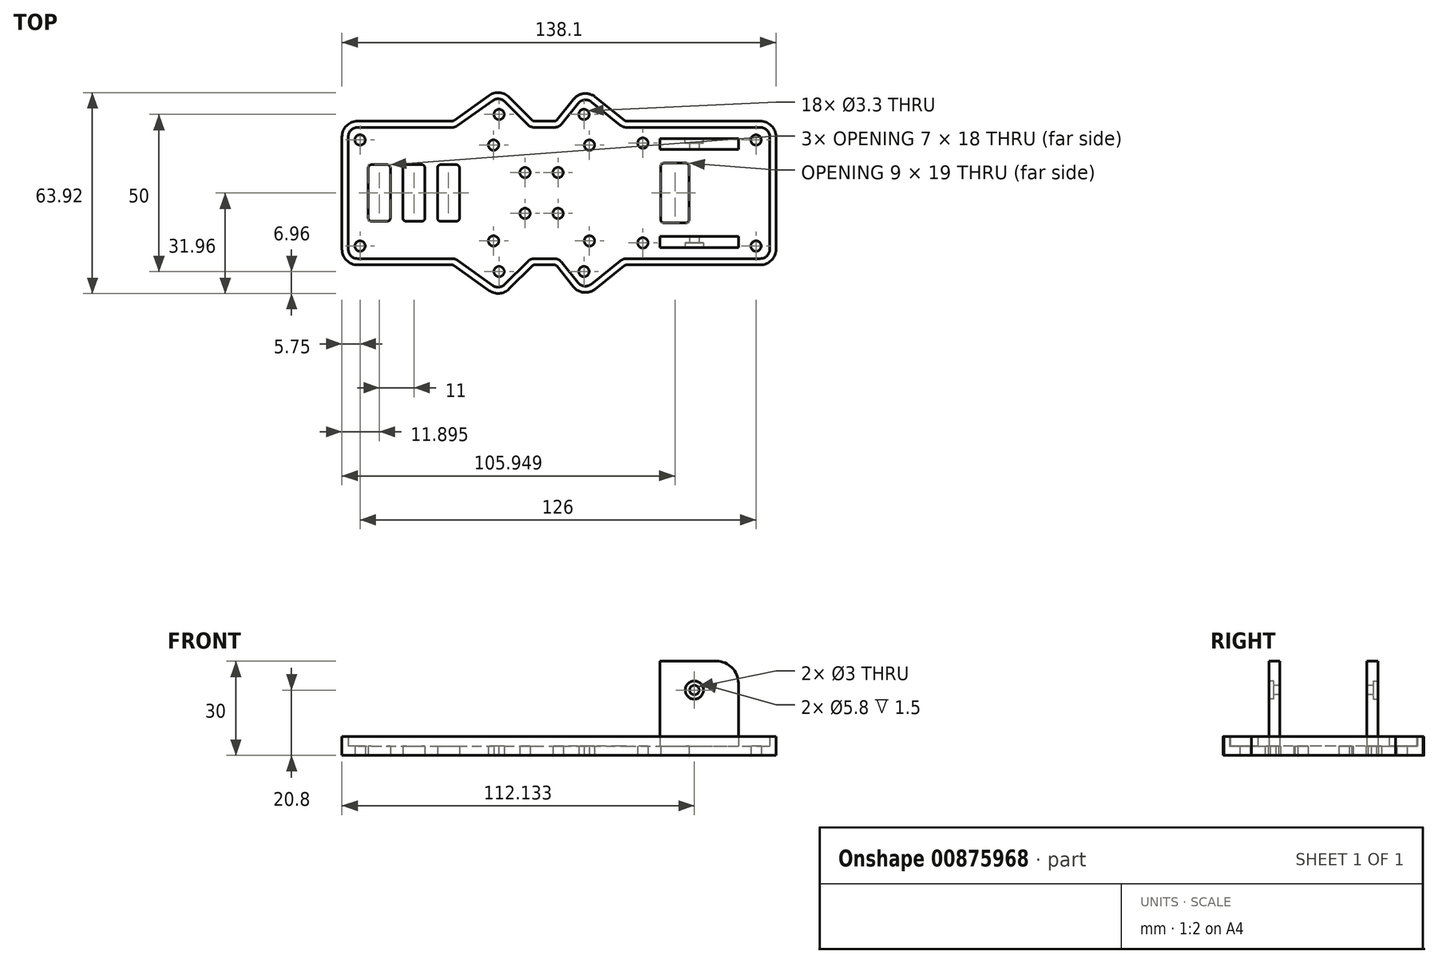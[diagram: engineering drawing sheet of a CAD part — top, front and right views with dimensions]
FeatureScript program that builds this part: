
annotation { "Feature Type Name" : "Feature", "Feature Type Description" : "" }
export const myFeature = defineFeature(function(context is Context, id is Id, definition is map)
    precondition{}
    {
        {
            var Q0;
            Q0=qCreatedBy(makeId("Top.planeOp"),FACE);
            var sketch = newSketch(context, id + "F0", { "sketchPlane" : qUnion([Q0])});
            skLineSegment(sketch, "E0.bottom", {"start": v(-58.5, 20.88) * mm, "end": v(-28.46, 20.88) * mm});
            skLineSegment(sketch, "E0.top", {"start": v(-58.5, -20.88) * mm, "end": v(-28.46, -20.88) * mm});
            skLineSegment(sketch, "E0.left", {"start": v(-61.5, 17.88) * mm, "end": v(-61.5, -17.88) * mm});
            skLineSegment(sketch, "E0.right", {"start": v(72.6, 17.88) * mm, "end": v(72.6, -17.88) * mm});
            skCircle(sketch, "E1", {"center": v(-5.25, 6.5) * mm, "radius": 1.65 * mm});
            skCircle(sketch, "E2.1.0.0", {"center": v(5.25, 6.5) * mm, "radius": 1.65 * mm});
            skCircle(sketch, "E3.0.1.0", {"center": v(-5.25, -6.5) * mm, "radius": 1.65 * mm});
            skCircle(sketch, "E3.0.1.1", {"center": v(5.25, -6.5) * mm, "radius": 1.65 * mm});
            skCircle(sketch, "E4", {"center": v(-15.25, 15.25) * mm, "radius": 1.65 * mm});
            skCircle(sketch, "E5", {"center": v(15.25, 15.25) * mm, "radius": 1.65 * mm});
            skCircle(sketch, "E6", {"center": v(15.25, -15.25) * mm, "radius": 1.65 * mm});
            skCircle(sketch, "E7", {"center": v(-15.25, -15.25) * mm, "radius": 1.65 * mm});
            skCircle(sketch, "E8", {"center": v(-13.5, 25) * mm, "radius": 1.65 * mm});
            skCircle(sketch, "E9.0.1.0", {"center": v(-13.5, -25) * mm, "radius": 1.65 * mm});
            skCircle(sketch, "E9.1.0.0", {"center": v(13.5, 25) * mm, "radius": 1.65 * mm});
            skCircle(sketch, "E9.1.1.0", {"center": v(13.5, -25) * mm, "radius": 1.65 * mm});
            skLineSegment(sketch, "E9.direction1", {"start": v(-13.5, 25) * mm, "end": v(13.5, 25) * mm, "construction": true});
            skLineSegment(sketch, "E9.direction2", {"start": v(-13.5, 25) * mm, "end": v(-13.5, -25) * mm, "construction": true});
            skCircle(sketch, "E10", {"center": v(-57.75, 16.88) * mm, "radius": 1.65 * mm});
            skCircle(sketch, "E11.0.1.0", {"center": v(-57.75, -16.88) * mm, "radius": 1.65 * mm});
            skLineSegment(sketch, "E11.direction2", {"start": v(-57.75, 16.88) * mm, "end": v(-57.75, -16.88) * mm, "construction": true});
            skLineSegment(sketch, "E12", {"start": v(-26.72, 21.43) * mm, "end": v(-15.57, 29.4) * mm});
            skLineSegment(sketch, "E13", {"start": v(-11.7, 29.08) * mm, "end": v(-4.38, 21.75) * mm});
            skLineSegment(sketch, "E14", {"start": v(-2.26, 20.88) * mm, "end": v(4.1, 20.88) * mm});
            skLineSegment(sketch, "E15", {"start": v(6.45, 22) * mm, "end": v(11.67, 28.53) * mm});
            skLineSegment(sketch, "E16", {"start": v(15.9, 29) * mm, "end": v(25.16, 21.54) * mm});
            skLineSegment(sketch, "E17.trimOffspring", {"start": v(27.04, 20.88) * mm, "end": v(69.6, 20.88) * mm});
            skLineSegment(sketch, "E18", {"start": v(-26.72, -21.43) * mm, "end": v(-15.57, -29.4) * mm});
            skLineSegment(sketch, "E19", {"start": v(-11.7, -29.08) * mm, "end": v(-4.38, -21.75) * mm});
            skLineSegment(sketch, "E20", {"start": v(25.16, -21.53) * mm, "end": v(15.85, -29) * mm});
            skLineSegment(sketch, "E21", {"start": v(11.63, -28.52) * mm, "end": v(6.45, -22) * mm});
            skLineSegment(sketch, "E22.trimOffspring", {"start": v(-2.26, -20.88) * mm, "end": v(4.1, -20.88) * mm});
            skLineSegment(sketch, "E23.trimOffspring", {"start": v(27.04, -20.88) * mm, "end": v(69.6, -20.88) * mm});
            skPoint(sketch, "E24.visualSharp", {"position": v(-61.5, 20.88) * mm});
            skArc(sketch, "E24.filletArc", {"start": v(-58.5, 20.88) * mm, "mid": v(-60.62, 20) * mm, "end": v(-61.5, 17.88) * mm});
            skPoint(sketch, "E25.visualSharp", {"position": v(-61.5, -20.88) * mm});
            skArc(sketch, "E25.filletArc", {"start": v(-61.5, -17.88) * mm, "mid": v(-60.62, -20) * mm, "end": v(-58.5, -20.88) * mm});
            skPoint(sketch, "E26.visualSharp", {"position": v(-27.5, 20.88) * mm});
            skArc(sketch, "E26.filletArc", {"start": v(-28.46, 20.88) * mm, "mid": v(-27.55, 21.02) * mm, "end": v(-26.72, 21.43) * mm});
            skPoint(sketch, "E27.visualSharp", {"position": v(-27.5, -20.88) * mm});
            skArc(sketch, "E27.filletArc", {"start": v(-26.72, -21.43) * mm, "mid": v(-27.55, -21.02) * mm, "end": v(-28.46, -20.88) * mm});
            skPoint(sketch, "E28.visualSharp", {"position": v(-13.5, -30.88) * mm});
            skArc(sketch, "E28.filletArc", {"start": v(-15.57, -29.4) * mm, "mid": v(-13.58, -29.95) * mm, "end": v(-11.7, -29.08) * mm});
            skPoint(sketch, "E29.visualSharp", {"position": v(-3.5, -20.88) * mm});
            skArc(sketch, "E29.filletArc", {"start": v(-2.26, -20.88) * mm, "mid": v(-3.4, -21.1) * mm, "end": v(-4.38, -21.75) * mm});
            skPoint(sketch, "E30.visualSharp", {"position": v(5.55, -20.88) * mm});
            skArc(sketch, "E30.filletArc", {"start": v(6.45, -22) * mm, "mid": v(5.4, -21.17) * mm, "end": v(4.1, -20.88) * mm});
            skPoint(sketch, "E31.visualSharp", {"position": v(13.5, -30.88) * mm});
            skArc(sketch, "E31.filletArc", {"start": v(11.63, -28.52) * mm, "mid": v(13.64, -29.63) * mm, "end": v(15.85, -29) * mm});
            skPoint(sketch, "E32.visualSharp", {"position": v(25.99, -20.88) * mm});
            skArc(sketch, "E32.filletArc", {"start": v(27.04, -20.88) * mm, "mid": v(26.05, -21.04) * mm, "end": v(25.16, -21.53) * mm});
            skPoint(sketch, "E33.visualSharp", {"position": v(-3.5, 20.88) * mm});
            skArc(sketch, "E33.filletArc", {"start": v(-4.38, 21.75) * mm, "mid": v(-3.4, 21.1) * mm, "end": v(-2.26, 20.88) * mm});
            skPoint(sketch, "E34.visualSharp", {"position": v(5.55, 20.88) * mm});
            skArc(sketch, "E34.filletArc", {"start": v(4.1, 20.88) * mm, "mid": v(5.4, 21.17) * mm, "end": v(6.45, 22) * mm});
            skPoint(sketch, "E35.visualSharp", {"position": v(13.55, 30.88) * mm});
            skArc(sketch, "E35.filletArc", {"start": v(15.9, 29) * mm, "mid": v(13.69, 29.63) * mm, "end": v(11.67, 28.53) * mm});
            skPoint(sketch, "E36.visualSharp", {"position": v(25.99, 20.88) * mm});
            skArc(sketch, "E36.filletArc", {"start": v(25.16, 21.54) * mm, "mid": v(26.05, 21.05) * mm, "end": v(27.04, 20.88) * mm});
            skPoint(sketch, "E37.visualSharp", {"position": v(72.6, 20.88) * mm});
            skArc(sketch, "E37.filletArc", {"start": v(72.6, 17.88) * mm, "mid": v(71.72, 20) * mm, "end": v(69.6, 20.88) * mm});
            skPoint(sketch, "E38.visualSharp", {"position": v(72.6, -20.87) * mm});
            skArc(sketch, "E38.filletArc", {"start": v(69.6, -20.87) * mm, "mid": v(71.72, -20) * mm, "end": v(72.6, -17.88) * mm});
            skPoint(sketch, "E39.visualSharp", {"position": v(-13.5, 30.88) * mm});
            skArc(sketch, "E39.filletArc", {"start": v(-11.7, 29.08) * mm, "mid": v(-13.58, 29.95) * mm, "end": v(-15.57, 29.4) * mm});
            skCircle(sketch, "E40", {"center": v(32.25, 15.88) * mm, "radius": 1.65 * mm});
            skCircle(sketch, "E41", {"center": v(68.25, 16.88) * mm, "radius": 1.65 * mm});
            skCircle(sketch, "E42.0.1.0", {"center": v(32.25, -15.88) * mm, "radius": 1.65 * mm});
            skLineSegment(sketch, "E42.direction1", {"start": v(32.25, 15.88) * mm, "end": v(39.65, 15.88) * mm, "construction": true});
            skLineSegment(sketch, "E42.direction2", {"start": v(32.25, 15.88) * mm, "end": v(32.25, -15.88) * mm, "construction": true});
            skCircle(sketch, "E43.0.1.0", {"center": v(68.25, -16.88) * mm, "radius": 1.65 * mm});
            skLineSegment(sketch, "E43.direction1", {"start": v(68.25, 16.88) * mm, "end": v(93.25, 16.88) * mm, "construction": true});
            skLineSegment(sketch, "E43.direction2", {"start": v(68.25, 16.88) * mm, "end": v(68.25, -16.88) * mm, "construction": true});
            skArc(sketch, "E44.0", {"start": v(-58.5, 22.88) * mm, "mid": v(-62.04, 21.41) * mm, "end": v(-63.5, 17.88) * mm});
            skLineSegment(sketch, "E44.1", {"start": v(-63.5, 17.88) * mm, "end": v(-63.5, -17.88) * mm});
            skArc(sketch, "E44.2", {"start": v(-63.5, -17.88) * mm, "mid": v(-62.04, -21.41) * mm, "end": v(-58.5, -22.88) * mm});
            skLineSegment(sketch, "E44.3", {"start": v(-58.5, -22.88) * mm, "end": v(-28.46, -22.88) * mm});
            skArc(sketch, "E44.4", {"start": v(-27.88, -23.06) * mm, "mid": v(-28.16, -22.92) * mm, "end": v(-28.46, -22.87) * mm});
            skLineSegment(sketch, "E44.5", {"start": v(-27.88, -23.06) * mm, "end": v(-16.73, -31.03) * mm});
            skArc(sketch, "E44.6", {"start": v(-16.73, -31.03) * mm, "mid": v(-13.41, -31.94) * mm, "end": v(-10.29, -30.5) * mm});
            skLineSegment(sketch, "E44.7", {"start": v(-10.29, -30.5) * mm, "end": v(-2.96, -23.17) * mm});
            skArc(sketch, "E44.8", {"start": v(-2.26, -22.88) * mm, "mid": v(-2.64, -22.95) * mm, "end": v(-2.96, -23.17) * mm});
            skLineSegment(sketch, "E44.9", {"start": v(17.15, 30.55) * mm, "end": v(26.42, 23.1) * mm});
            skArc(sketch, "E44.10", {"start": v(17.15, 30.55) * mm, "mid": v(13.47, 31.62) * mm, "end": v(10.1, 29.78) * mm});
            skLineSegment(sketch, "E44.11", {"start": v(4.89, 23.25) * mm, "end": v(10.1, 29.78) * mm});
            skArc(sketch, "E44.12", {"start": v(4.1, 22.88) * mm, "mid": v(4.54, 22.97) * mm, "end": v(4.89, 23.25) * mm});
            skLineSegment(sketch, "E44.13", {"start": v(-2.26, 22.88) * mm, "end": v(4.1, 22.88) * mm});
            skArc(sketch, "E44.14", {"start": v(-2.96, 23.17) * mm, "mid": v(-2.64, 22.95) * mm, "end": v(-2.26, 22.88) * mm});
            skArc(sketch, "E44.15", {"start": v(-28.46, 22.88) * mm, "mid": v(-28.16, 22.92) * mm, "end": v(-27.88, 23.06) * mm});
            skLineSegment(sketch, "E44.16", {"start": v(-27.88, 23.06) * mm, "end": v(-16.73, 31.03) * mm});
            skArc(sketch, "E44.17", {"start": v(-10.29, 30.5) * mm, "mid": v(-13.41, 31.94) * mm, "end": v(-16.73, 31.03) * mm});
            skLineSegment(sketch, "E44.18", {"start": v(-10.29, 30.5) * mm, "end": v(-2.96, 23.17) * mm});
            skArc(sketch, "E44.19", {"start": v(26.42, 23.1) * mm, "mid": v(26.71, 22.93) * mm, "end": v(27.04, 22.88) * mm});
            skLineSegment(sketch, "E44.20", {"start": v(27.04, 22.88) * mm, "end": v(69.6, 22.88) * mm});
            skArc(sketch, "E44.21", {"start": v(74.6, 17.88) * mm, "mid": v(73.14, 21.41) * mm, "end": v(69.6, 22.88) * mm});
            skLineSegment(sketch, "E44.22", {"start": v(74.6, 17.88) * mm, "end": v(74.6, -17.88) * mm});
            skArc(sketch, "E44.23", {"start": v(69.6, -22.88) * mm, "mid": v(73.14, -21.41) * mm, "end": v(74.6, -17.88) * mm});
            skLineSegment(sketch, "E44.24", {"start": v(27.04, -22.88) * mm, "end": v(69.6, -22.88) * mm});
            skArc(sketch, "E44.25", {"start": v(27.04, -22.88) * mm, "mid": v(26.7, -22.93) * mm, "end": v(26.41, -23.1) * mm});
            skLineSegment(sketch, "E44.26", {"start": v(26.41, -23.1) * mm, "end": v(17.1, -30.55) * mm});
            skArc(sketch, "E44.27", {"start": v(10.06, -29.76) * mm, "mid": v(13.42, -31.62) * mm, "end": v(17.1, -30.55) * mm});
            skLineSegment(sketch, "E44.28", {"start": v(-58.5, 22.88) * mm, "end": v(-28.46, 22.88) * mm});
            skLineSegment(sketch, "E44.29", {"start": v(10.06, -29.76) * mm, "end": v(4.89, -23.25) * mm});
            skArc(sketch, "E44.30", {"start": v(4.89, -23.25) * mm, "mid": v(4.54, -22.97) * mm, "end": v(4.1, -22.88) * mm});
            skLineSegment(sketch, "E44.31", {"start": v(-2.26, -22.88) * mm, "end": v(4.1, -22.88) * mm});
            skLineSegment(sketch, "E45.bottom", {"start": v(-54.1, 9) * mm, "end": v(-49.1, 9) * mm});
            skLineSegment(sketch, "E45.top", {"start": v(-54.1, -9) * mm, "end": v(-49.1, -9) * mm});
            skLineSegment(sketch, "E45.left", {"start": v(-55.1, 8) * mm, "end": v(-55.1, -8) * mm});
            skLineSegment(sketch, "E45.right", {"start": v(-48.1, 8) * mm, "end": v(-48.1, -8) * mm});
            skLineSegment(sketch, "E46.1.0.0", {"start": v(-44.1, 8) * mm, "end": v(-44.1, -8) * mm});
            skLineSegment(sketch, "E46.1.0.1", {"start": v(-43.1, 9) * mm, "end": v(-38.1, 9) * mm});
            skLineSegment(sketch, "E46.1.0.2", {"start": v(-37.1, 8) * mm, "end": v(-37.1, -8) * mm});
            skLineSegment(sketch, "E46.1.0.3", {"start": v(-43.1, -9) * mm, "end": v(-38.1, -9) * mm});
            skLineSegment(sketch, "E46.2.0.0", {"start": v(-33.1, 8) * mm, "end": v(-33.1, -8) * mm});
            skLineSegment(sketch, "E46.2.0.1", {"start": v(-32.1, 9) * mm, "end": v(-27.1, 9) * mm});
            skLineSegment(sketch, "E46.2.0.2", {"start": v(-26.1, 8) * mm, "end": v(-26.1, -8) * mm});
            skLineSegment(sketch, "E46.2.0.3", {"start": v(-32.1, -9) * mm, "end": v(-27.1, -9) * mm});
            skLineSegment(sketch, "E46.direction1", {"start": v(-55.1, -9) * mm, "end": v(-44.1, -9) * mm, "construction": true});
            skPoint(sketch, "E47.visualSharp", {"position": v(-55.1, 9) * mm});
            skArc(sketch, "E47.filletArc", {"start": v(-54.1, 9) * mm, "mid": v(-54.81, 8.7) * mm, "end": v(-55.1, 8) * mm});
            skPoint(sketch, "E48.visualSharp", {"position": v(-48.1, 9) * mm});
            skArc(sketch, "E48.filletArc", {"start": v(-48.1, 8) * mm, "mid": v(-48.4, 8.7) * mm, "end": v(-49.1, 9) * mm});
            skPoint(sketch, "E49.visualSharp", {"position": v(-55.1, -9) * mm});
            skArc(sketch, "E49.filletArc", {"start": v(-55.1, -8) * mm, "mid": v(-54.81, -8.7) * mm, "end": v(-54.1, -9) * mm});
            skPoint(sketch, "E50.visualSharp", {"position": v(-48.1, -9) * mm});
            skArc(sketch, "E50.filletArc", {"start": v(-49.1, -9) * mm, "mid": v(-48.4, -8.7) * mm, "end": v(-48.1, -8) * mm});
            skPoint(sketch, "E51.visualSharp", {"position": v(-44.1, 9) * mm});
            skArc(sketch, "E51.filletArc", {"start": v(-43.1, 9) * mm, "mid": v(-43.81, 8.7) * mm, "end": v(-44.1, 8) * mm});
            skPoint(sketch, "E52.visualSharp", {"position": v(-37.1, 9) * mm});
            skArc(sketch, "E52.filletArc", {"start": v(-37.1, 8) * mm, "mid": v(-37.4, 8.7) * mm, "end": v(-38.1, 9) * mm});
            skPoint(sketch, "E53.visualSharp", {"position": v(-44.1, -9) * mm});
            skArc(sketch, "E53.filletArc", {"start": v(-44.1, -8) * mm, "mid": v(-43.81, -8.7) * mm, "end": v(-43.1, -9) * mm});
            skPoint(sketch, "E54.visualSharp", {"position": v(-37.1, -9) * mm});
            skArc(sketch, "E54.filletArc", {"start": v(-38.1, -9) * mm, "mid": v(-37.4, -8.7) * mm, "end": v(-37.1, -8) * mm});
            skPoint(sketch, "E55.visualSharp", {"position": v(-33.1, -9) * mm});
            skArc(sketch, "E55.filletArc", {"start": v(-33.1, -8) * mm, "mid": v(-32.81, -8.7) * mm, "end": v(-32.1, -9) * mm});
            skPoint(sketch, "E56.visualSharp", {"position": v(-26.1, -9) * mm});
            skArc(sketch, "E56.filletArc", {"start": v(-27.1, -9) * mm, "mid": v(-26.4, -8.7) * mm, "end": v(-26.1, -8) * mm});
            skPoint(sketch, "E57.visualSharp", {"position": v(-26.1, 9) * mm});
            skArc(sketch, "E57.filletArc", {"start": v(-26.1, 8) * mm, "mid": v(-26.4, 8.7) * mm, "end": v(-27.1, 9) * mm});
            skPoint(sketch, "E58.visualSharp", {"position": v(-33.1, 9) * mm});
            skArc(sketch, "E58.filletArc", {"start": v(-32.1, 9) * mm, "mid": v(-32.81, 8.7) * mm, "end": v(-33.1, 8) * mm});
            skLineSegment(sketch, "E59.bottom", {"start": v(38.95, 9.5) * mm, "end": v(45.95, 9.5) * mm});
            skLineSegment(sketch, "E59.top", {"start": v(38.95, -9.5) * mm, "end": v(45.95, -9.5) * mm});
            skLineSegment(sketch, "E59.left", {"start": v(37.95, 8.5) * mm, "end": v(37.95, -8.5) * mm});
            skLineSegment(sketch, "E59.right", {"start": v(46.95, 8.5) * mm, "end": v(46.95, -8.5) * mm});
            skPoint(sketch, "E60.visualSharp", {"position": v(37.95, 9.5) * mm});
            skArc(sketch, "E60.filletArc", {"start": v(38.95, 9.5) * mm, "mid": v(38.24, 9.2) * mm, "end": v(37.95, 8.5) * mm});
            skPoint(sketch, "E61.visualSharp", {"position": v(46.95, 9.5) * mm});
            skArc(sketch, "E61.filletArc", {"start": v(46.95, 8.5) * mm, "mid": v(46.66, 9.2) * mm, "end": v(45.95, 9.5) * mm});
            skPoint(sketch, "E62.visualSharp", {"position": v(46.95, -9.5) * mm});
            skArc(sketch, "E62.filletArc", {"start": v(45.95, -9.5) * mm, "mid": v(46.66, -9.2) * mm, "end": v(46.95, -8.5) * mm});
            skPoint(sketch, "E63.visualSharp", {"position": v(37.95, -9.5) * mm});
            skArc(sketch, "E63.filletArc", {"start": v(37.95, -8.5) * mm, "mid": v(38.24, -9.2) * mm, "end": v(38.95, -9.5) * mm});
            skSolve(sketch);
        }
        {
            var Q0;
            Q0=makeQuery(id+"F0.imprint","IMPRINT",FACE,{"disambiguationData":[TD([[makeQuery(id+"F0.imprint","IMPRINT",EDGE,{"derivedFrom":sQuery(id+"F0.wireOp",EDGE,"E0.bottom")}),-1.0]])]});
            extrude(context, id + "F1", {"entities" : qUnion([Q0]), "depth" : 3 * mm, "offsetDistance" : 25 * mm});
        }
        {
            var Q0;
            Q0=makeQuery(id+"F0.imprint","IMPRINT",FACE,{"disambiguationData":[TD([[makeQuery(id+"F0.imprint","IMPRINT",EDGE,{"derivedFrom":sQuery(id+"F0.wireOp",EDGE,"E0.bottom")}),1.0]])]});
            extrude(context, id + "F2", {"entities" : qUnion([Q0]), "operationType" : NewBodyOperationType.ADD, "depth" : 6 * mm, "offsetDistance" : 25 * mm});
        }
        {
            var Q0;
            Q0=makeQuery(id+"F1.opExtrude","CAP_FACE",FACE,{"disambiguationData":[OSD([sQuery(id+"F0.wireOp",EDGE,"E0.bottom"),sQuery(id+"F0.wireOp",EDGE,"E0.top"),sQuery(id+"F0.wireOp",EDGE,"E0.left"),sQuery(id+"F0.wireOp",EDGE,"E0.right"),sQuery(id+"F0.wireOp",EDGE,"E1"),sQuery(id+"F0.wireOp",EDGE,"E2.1.0.0"),sQuery(id+"F0.wireOp",EDGE,"E3.0.1.0"),sQuery(id+"F0.wireOp",EDGE,"E3.0.1.1"),sQuery(id+"F0.wireOp",EDGE,"E4"),sQuery(id+"F0.wireOp",EDGE,"E5"),sQuery(id+"F0.wireOp",EDGE,"E6"),sQuery(id+"F0.wireOp",EDGE,"E7"),sQuery(id+"F0.wireOp",EDGE,"E8"),sQuery(id+"F0.wireOp",EDGE,"E9.0.1.0"),sQuery(id+"F0.wireOp",EDGE,"E9.1.0.0"),sQuery(id+"F0.wireOp",EDGE,"E9.1.1.0"),sQuery(id+"F0.wireOp",EDGE,"E10"),sQuery(id+"F0.wireOp",EDGE,"E11.0.1.0"),sQuery(id+"F0.wireOp",EDGE,"E12"),sQuery(id+"F0.wireOp",EDGE,"E13"),sQuery(id+"F0.wireOp",EDGE,"E14"),sQuery(id+"F0.wireOp",EDGE,"E15"),sQuery(id+"F0.wireOp",EDGE,"E16"),sQuery(id+"F0.wireOp",EDGE,"E17.trimOffspring"),sQuery(id+"F0.wireOp",EDGE,"E18"),sQuery(id+"F0.wireOp",EDGE,"E19"),sQuery(id+"F0.wireOp",EDGE,"E20"),sQuery(id+"F0.wireOp",EDGE,"E21"),sQuery(id+"F0.wireOp",EDGE,"E22.trimOffspring"),sQuery(id+"F0.wireOp",EDGE,"E23.trimOffspring"),sQuery(id+"F0.wireOp",EDGE,"E24.filletArc"),sQuery(id+"F0.wireOp",EDGE,"E25.filletArc"),sQuery(id+"F0.wireOp",EDGE,"E26.filletArc"),sQuery(id+"F0.wireOp",EDGE,"E27.filletArc"),sQuery(id+"F0.wireOp",EDGE,"E28.filletArc"),sQuery(id+"F0.wireOp",EDGE,"E29.filletArc"),sQuery(id+"F0.wireOp",EDGE,"E30.filletArc"),sQuery(id+"F0.wireOp",EDGE,"E31.filletArc"),sQuery(id+"F0.wireOp",EDGE,"E32.filletArc"),sQuery(id+"F0.wireOp",EDGE,"E33.filletArc"),sQuery(id+"F0.wireOp",EDGE,"E34.filletArc"),sQuery(id+"F0.wireOp",EDGE,"E35.filletArc"),sQuery(id+"F0.wireOp",EDGE,"E36.filletArc"),sQuery(id+"F0.wireOp",EDGE,"E37.filletArc"),sQuery(id+"F0.wireOp",EDGE,"E38.filletArc"),sQuery(id+"F0.wireOp",EDGE,"E39.filletArc"),sQuery(id+"F0.wireOp",EDGE,"E40"),sQuery(id+"F0.wireOp",EDGE,"E41"),sQuery(id+"F0.wireOp",EDGE,"E42.0.1.0"),sQuery(id+"F0.wireOp",EDGE,"E43.0.1.0"),sQuery(id+"F0.wireOp",EDGE,"E45.bottom"),sQuery(id+"F0.wireOp",EDGE,"E45.top"),sQuery(id+"F0.wireOp",EDGE,"E45.left"),sQuery(id+"F0.wireOp",EDGE,"E45.right"),sQuery(id+"F0.wireOp",EDGE,"E46.1.0.0"),sQuery(id+"F0.wireOp",EDGE,"E46.1.0.1"),sQuery(id+"F0.wireOp",EDGE,"E46.1.0.2"),sQuery(id+"F0.wireOp",EDGE,"E46.1.0.3"),sQuery(id+"F0.wireOp",EDGE,"E46.2.0.0"),sQuery(id+"F0.wireOp",EDGE,"E46.2.0.1"),sQuery(id+"F0.wireOp",EDGE,"E46.2.0.2"),sQuery(id+"F0.wireOp",EDGE,"E46.2.0.3"),sQuery(id+"F0.wireOp",EDGE,"E47.filletArc"),sQuery(id+"F0.wireOp",EDGE,"E48.filletArc"),sQuery(id+"F0.wireOp",EDGE,"E49.filletArc"),sQuery(id+"F0.wireOp",EDGE,"E50.filletArc"),sQuery(id+"F0.wireOp",EDGE,"E51.filletArc"),sQuery(id+"F0.wireOp",EDGE,"E52.filletArc"),sQuery(id+"F0.wireOp",EDGE,"E53.filletArc"),sQuery(id+"F0.wireOp",EDGE,"E54.filletArc"),sQuery(id+"F0.wireOp",EDGE,"E55.filletArc"),sQuery(id+"F0.wireOp",EDGE,"E56.filletArc"),sQuery(id+"F0.wireOp",EDGE,"E57.filletArc"),sQuery(id+"F0.wireOp",EDGE,"E58.filletArc"),sQuery(id+"F0.wireOp",EDGE,"E59.bottom"),sQuery(id+"F0.wireOp",EDGE,"E59.top"),sQuery(id+"F0.wireOp",EDGE,"E59.left"),sQuery(id+"F0.wireOp",EDGE,"E59.right"),sQuery(id+"F0.wireOp",EDGE,"E60.filletArc"),sQuery(id+"F0.wireOp",EDGE,"E61.filletArc"),sQuery(id+"F0.wireOp",EDGE,"E62.filletArc"),sQuery(id+"F0.wireOp",EDGE,"E63.filletArc")])],"isStart":false});
            var sketch = newSketch(context, id + "F3", { "sketchPlane" : qUnion([Q0])});
            skLineSegment(sketch, "E64.bottom", {"start": v(37.63, 17.35) * mm, "end": v(62.63, 17.35) * mm});
            skLineSegment(sketch, "E64.top", {"start": v(37.63, 13.85) * mm, "end": v(62.63, 13.85) * mm});
            skLineSegment(sketch, "E64.left", {"start": v(37.63, 17.35) * mm, "end": v(37.63, 13.85) * mm});
            skLineSegment(sketch, "E64.right", {"start": v(62.63, 17.35) * mm, "end": v(62.63, 13.85) * mm});
            skLineSegment(sketch, "E65.MirrorCS", {"start": v(37.63, -13.85) * mm, "end": v(62.63, -13.85) * mm});
            skLineSegment(sketch, "E66.MirrorCS", {"start": v(37.63, -17.35) * mm, "end": v(37.63, -13.85) * mm});
            skLineSegment(sketch, "E67.MirrorCS", {"start": v(37.63, -17.35) * mm, "end": v(62.63, -17.35) * mm});
            skLineSegment(sketch, "E68.MirrorCS", {"start": v(62.63, -17.35) * mm, "end": v(62.63, -13.85) * mm});
            skSolve(sketch);
        }
        {
            var Q0;
            Q0=makeQuery(id+"F3.imprint","IMPRINT",FACE,{"disambiguationData":[TD([[makeQuery(id+"F3.imprint","IMPRINT",EDGE,{"derivedFrom":sQuery(id+"F3.wireOp",EDGE,"E64.bottom")}),-1.0]])]});
            var Q1;
            Q1=makeQuery(id+"F3.imprint","IMPRINT",FACE,{"disambiguationData":[TD([[makeQuery(id+"F3.imprint","IMPRINT",EDGE,{"derivedFrom":sQuery(id+"F3.wireOp",EDGE,"E65.MirrorCS")}),-1.0]])]});
            var Q2;
            Q2=sQuery(id+"F3.wireOp",EDGE,"E64.bottom");
            var Q3;
            Q3=sQuery(id+"F3.wireOp",EDGE,"E64.top");
            var Q4;
            Q4=sQuery(id+"F3.wireOp",EDGE,"E64.left");
            var Q5;
            Q5=sQuery(id+"F3.wireOp",EDGE,"E64.right");
            var Q6;
            Q6=sQuery(id+"F3.wireOp",EDGE,"E67.MirrorCS");
            var Q7;
            Q7=sQuery(id+"F3.wireOp",EDGE,"E68.MirrorCS");
            var Q8;
            Q8=sQuery(id+"F3.wireOp",EDGE,"E65.MirrorCS");
            var Q9;
            Q9=sQuery(id+"F3.wireOp",EDGE,"E66.MirrorCS");
            extrude(context, id + "F4", {"entities" : qUnion([Q0, Q1]), "surfaceEntities" : qUnion([Q2, Q3, Q4, Q5, Q6, Q7, Q8, Q9]), "depth" : 27 * mm, "offsetDistance" : 25 * mm});
        }
        {
            var Q0;
            Q0=makeQuery(id+"F4.opExtrude","CAP_EDGE",EDGE,{"disambiguationData":[OSD([sQuery(id+"F3.wireOp",EDGE,"E64.right")])],"isStart":false});
            var Q1;
            Q1=makeQuery(id+"F4.opExtrude","CAP_EDGE",EDGE,{"disambiguationData":[OSD([sQuery(id+"F3.wireOp",EDGE,"E68.MirrorCS")])],"isStart":false});
            fillet(context, id + "F5", {"entities" : qUnion([Q0, Q1]), "radius" : 7 * mm, "tangentPropagation" : true, "allowEdgeOverflow" : false});
        }
        {
            var Q0;
            Q0=makeQuery(id+"F4.opExtrude","SWEPT_FACE",FACE,{"disambiguationData":[OSD([sQuery(id+"F3.wireOp",EDGE,"E67.MirrorCS")])]});
            var sketch = newSketch(context, id + "F6", { "sketchPlane" : qUnion([Q0])});
            skCircle(sketch, "E69", {"center": v(48.63, 20.8) * mm, "radius": 1.5 * mm});
            skCircle(sketch, "E70.0", {"center": v(48.63, 20.8) * mm, "radius": 2.9 * mm});
            skSolve(sketch);
        }
        {
            var Q0;
            Q0=sQuery(id+"F6.wireOp",VERTEX,"E69.center");
            var Q1;
            Q1=makeQuery(id+"F4.opExtrude","SWEPT_BODY",BODY,{"disambiguationData":[OSD([sQuery(id+"F3.wireOp",EDGE,"E64.bottom"),sQuery(id+"F3.wireOp",EDGE,"E64.top"),sQuery(id+"F3.wireOp",EDGE,"E64.left"),sQuery(id+"F3.wireOp",EDGE,"E64.right")])]});
            var Q2;
            Q2=makeQuery(id+"F4.opExtrude","SWEPT_BODY",BODY,{"disambiguationData":[OSD([sQuery(id+"F3.wireOp",EDGE,"E65.MirrorCS"),sQuery(id+"F3.wireOp",EDGE,"E66.MirrorCS"),sQuery(id+"F3.wireOp",EDGE,"E67.MirrorCS"),sQuery(id+"F3.wireOp",EDGE,"E68.MirrorCS")])]});
            hole(context, id + "F7", {"style" : HoleStyle.SIMPLE, "endStyle" : HoleEndStyle.THROUGH, "holeDiameter" : 3 * mm, "majorDiameter" : 5 * mm, "isTappedThrough" : true, "tappedDepth" : 12 * mm, "tapClearance" : 3, "locations" : qUnion([Q0]), "scope" : qUnion([Q1, Q2])});
        }
        {
            var Q0;
            Q0=makeQuery(id+"F6.imprint","IMPRINT",FACE,{"disambiguationData":[TD([[makeQuery(id+"F6.imprint","IMPRINT",EDGE,{"derivedFrom":sQuery(id+"F6.wireOp",EDGE,"E69")}),-1.0]])]});
            extrude(context, id + "F8", {"entities" : qUnion([Q0]), "operationType" : NewBodyOperationType.REMOVE, "oppositeDirection" : true, "depth" : 1.5 * mm, "offsetDistance" : 25 * mm});
        }
        {
            var Q0;
            Q0=makeQuery(id+"F4.opExtrude","SWEPT_FACE",FACE,{"disambiguationData":[OSD([sQuery(id+"F3.wireOp",EDGE,"E64.bottom")])]});
            var sketch = newSketch(context, id + "F9", { "sketchPlane" : qUnion([Q0])});
            skCircle(sketch, "E71.0", {"center": v(-48.63, 20.8) * mm, "radius": 2.9 * mm});
            skSolve(sketch);
        }
        {
            var Q0;
            Q0=makeQuery(id+"F9.imprint","IMPRINT",FACE,{"disambiguationData":[TD([[makeQuery(id+"F9.imprint","IMPRINT",EDGE,{"derivedFrom":sQuery(id+"F9.wireOp",EDGE,"E71.0")}),1.0]])]});
            extrude(context, id + "F10", {"entities" : qUnion([Q0]), "operationType" : NewBodyOperationType.REMOVE, "oppositeDirection" : true, "depth" : 1.5 * mm, "offsetDistance" : 25 * mm});
        }
    });
